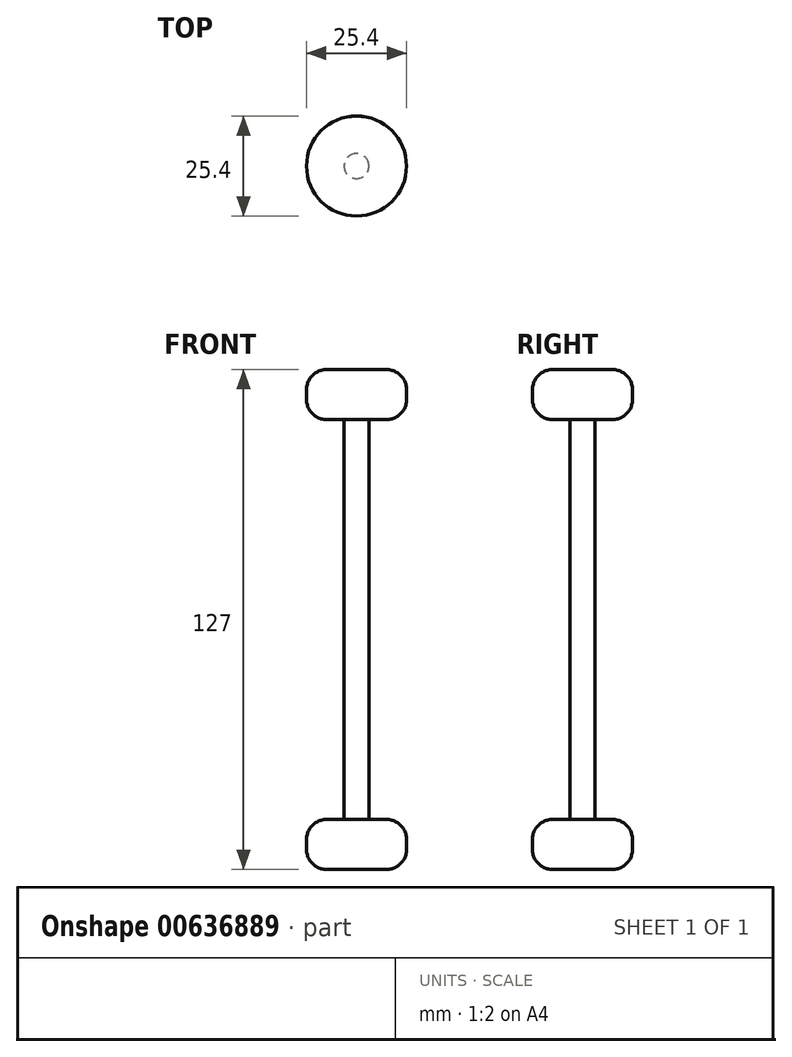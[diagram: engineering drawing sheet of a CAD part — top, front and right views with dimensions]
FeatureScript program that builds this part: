
annotation { "Feature Type Name" : "Feature", "Feature Type Description" : "" }
export const myFeature = defineFeature(function(context is Context, id is Id, definition is map)
    precondition{}
    {
        {
            var Q0;
            Q0=qCreatedBy(makeId("Top.planeOp"),FACE);
            var sketch = newSketch(context, id + "F0", { "sketchPlane" : qUnion([Q0])});
            skCircle(sketch, "E0", {"center": v(0, 0) * mm, "radius": 12.7 * mm});
            skSolve(sketch);
        }
        {
            var Q0;
            Q0 = qSketchRegion(id + "F0", true);
            extrude(context, id + "F1", {"entities" : qUnion([Q0]), "depth" : 12.7 * mm, "offsetDistance" : 25.4 * mm});
        }
        {
            var Q0;
            Q0=makeQuery(id+"F1.opExtrude","CAP_FACE",FACE,{"disambiguationData":[OSD([sQuery(id+"F0.wireOp",EDGE,"E0")])],"isStart":false});
            var sketch = newSketch(context, id + "F2", { "sketchPlane" : qUnion([Q0])});
            skCircle(sketch, "E1", {"center": v(0, 0) * mm, "radius": 3.18 * mm});
            skSolve(sketch);
        }
        {
            var Q0;
            Q0 = qSketchRegion(id + "F2", true);
            extrude(context, id + "F3", {"entities" : qUnion([Q0]), "operationType" : NewBodyOperationType.ADD, "depth" : 101.6 * mm, "offsetDistance" : 25.4 * mm});
        }
        {
            var Q0;
            Q0=makeQuery(id+"F3.opExtrude","CAP_FACE",FACE,{"disambiguationData":[OSD([sQuery(id+"F2.wireOp",EDGE,"E1")])],"isStart":false});
            var sketch = newSketch(context, id + "F4", { "sketchPlane" : qUnion([Q0])});
            skCircle(sketch, "E2", {"center": v(0, 0) * mm, "radius": 12.7 * mm});
            skSolve(sketch);
        }
        {
            var Q0;
            Q0 = qSketchRegion(id + "F4", true);
            extrude(context, id + "F5", {"entities" : qUnion([Q0]), "operationType" : NewBodyOperationType.ADD, "depth" : 12.7 * mm, "offsetDistance" : 25.4 * mm});
        }
        {
            var Q0;
            Q0=makeQuery(id+"F1.opExtrude","CAP_EDGE",EDGE,{"disambiguationData":[OSD([sQuery(id+"F0.wireOp",EDGE,"E0")])],"isStart":false});
            var Q1;
            Q1=makeQuery(id+"F1.opExtrude","CAP_EDGE",EDGE,{"disambiguationData":[OSD([sQuery(id+"F0.wireOp",EDGE,"E0")])],"isStart":true});
            var Q2;
            Q2=makeQuery(id+"F5.opExtrude","CAP_EDGE",EDGE,{"disambiguationData":[OSD([sQuery(id+"F4.wireOp",EDGE,"E2")])],"isStart":false});
            var Q3;
            Q3=makeQuery(id+"F5.opExtrude","CAP_EDGE",EDGE,{"disambiguationData":[OSD([sQuery(id+"F4.wireOp",EDGE,"E2")])],"isStart":true});
            fillet(context, id + "F6", {"entities" : qUnion([Q0, Q1, Q2, Q3]), "radius" : 5.08 * mm, "tangentPropagation" : true, "allowEdgeOverflow" : false});
        }
        {
            var Q0;
            Q0=makeQuery(id+"F1.opExtrude","SWEPT_BODY",BODY,{"disambiguationData":[OSD([sQuery(id+"F0.wireOp",EDGE,"E0")])]});
            transform(context, id + "F7", {"entities" : qUnion([Q0]), "transformType" : TransformType.TRANSLATION_3D, "dx" : 0 * mm, "dy" : 0 * mm, "dz" : -52.32 * mm, "makeCopy" : false});
        }
    });
